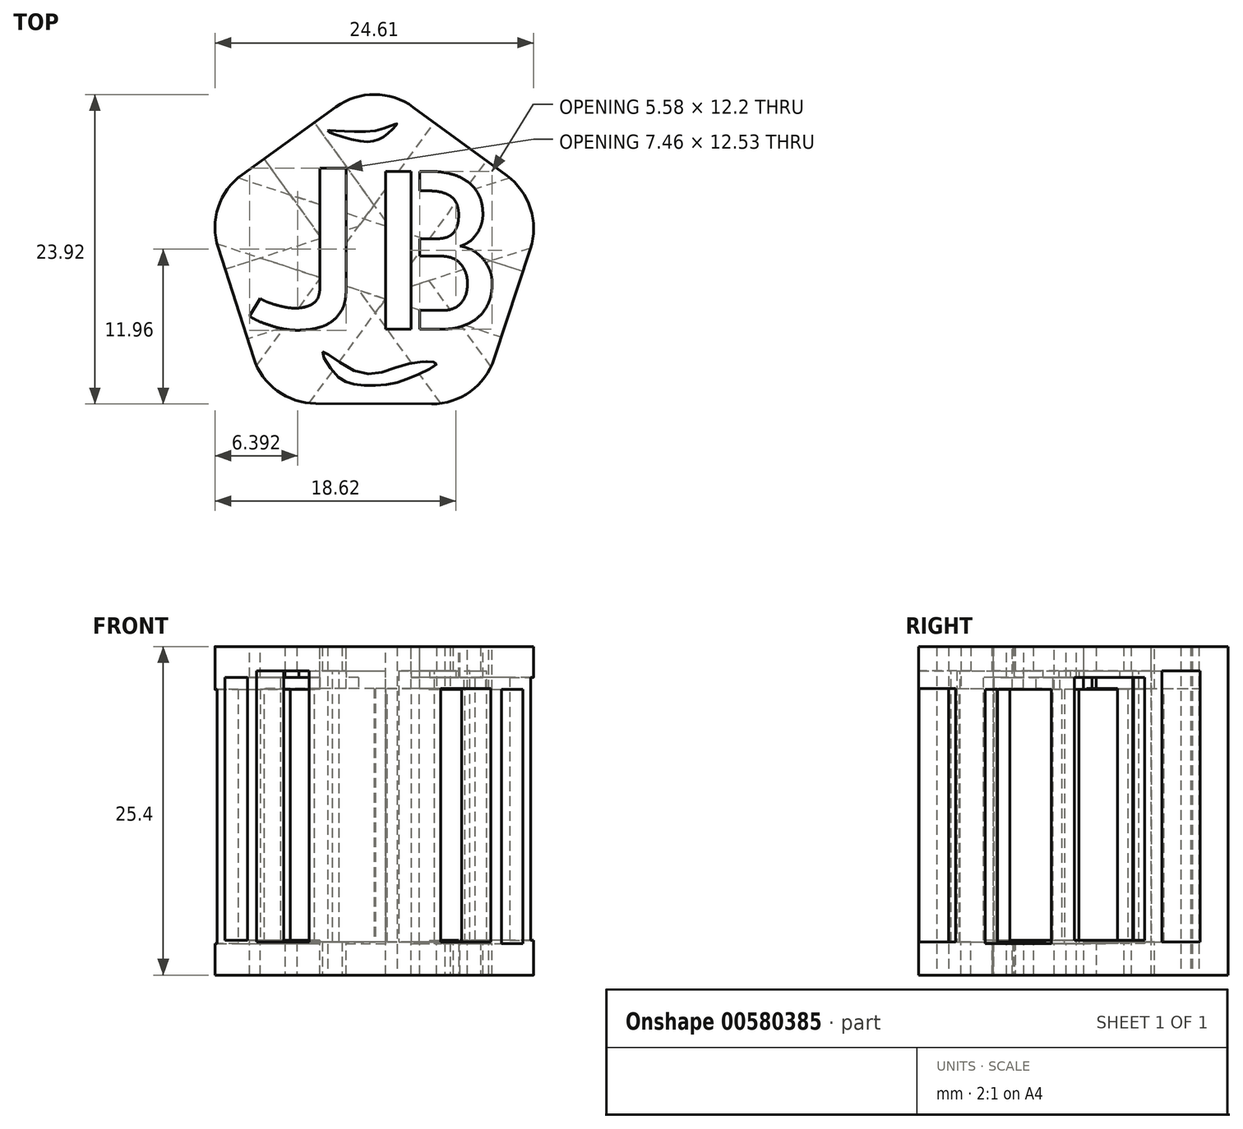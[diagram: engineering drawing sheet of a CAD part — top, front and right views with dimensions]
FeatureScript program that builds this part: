
annotation { "Feature Type Name" : "Feature", "Feature Type Description" : "" }
export const myFeature = defineFeature(function(context is Context, id is Id, definition is map)
    precondition{}
    {
        {
            var Q0;
            Q0=qCreatedBy(makeId("Top.planeOp"),FACE);
            var sketch = newSketch(context, id + "F0", { "sketchPlane" : qUnion([Q0])});
            skLineSegment(sketch, "E0.bottom", {"start": v(-11.35, 8.5) * mm, "end": v(14.05, 8.5) * mm});
            skLineSegment(sketch, "E0.top", {"start": v(-11.35, -16.9) * mm, "end": v(14.05, -16.9) * mm});
            skLineSegment(sketch, "E0.left", {"start": v(-11.35, 8.5) * mm, "end": v(-11.35, -16.9) * mm});
            skLineSegment(sketch, "E0.right", {"start": v(14.05, 8.5) * mm, "end": v(14.05, -16.9) * mm});
            skSolve(sketch);
        }
        {
            var Q0;
            Q0=makeQuery(id+"F0.imprint","IMPRINT",FACE,{"disambiguationData":[TD([[makeQuery(id+"F0.imprint","IMPRINT",EDGE,{"derivedFrom":sQuery(id+"F0.wireOp",EDGE,"E0.bottom")}),-1.0]])]});
            var sketch = newSketch(context, id + "F1", { "sketchPlane" : qUnion([Q0])});
            skCircle(sketch, "E1.cCircle", {"center": v(0, -4.14) * mm, "radius": 11.23 * mm, "construction": true});
            skLineSegment(sketch, "E1.0", {"start": v(0.05, 9.74) * mm, "end": v(13.21, 0.1) * mm});
            skLineSegment(sketch, "E1.1", {"start": v(13.21, 0.1) * mm, "end": v(8.12, -15.4) * mm});
            skLineSegment(sketch, "E1.2", {"start": v(8.12, -15.4) * mm, "end": v(-8.2, -15.34) * mm});
            skLineSegment(sketch, "E1.3", {"start": v(-8.2, -15.34) * mm, "end": v(-13.18, 0.2) * mm});
            skLineSegment(sketch, "E1.4", {"start": v(-13.18, 0.2) * mm, "end": v(0.05, 9.74) * mm});
            skPoint(sketch, "E1.0.midPoint", {"position": v(6.63, 4.92) * mm});
            skSolve(sketch);
        }
        {
            var Q0;
            Q0 = qSketchRegion(id + "F1", true);
            extrude(context, id + "F2", {"entities" : qUnion([Q0]), "depth" : 25.4 * mm, "offsetDistance" : 25.4 * mm});
        }
        {
            var Q0;
            Q0=makeQuery(id+"F2.opExtrude","CAP_FACE",FACE,{"disambiguationData":[OSD([sQuery(id+"F1.wireOp",EDGE,"E1.0"),sQuery(id+"F1.wireOp",EDGE,"E1.1"),sQuery(id+"F1.wireOp",EDGE,"E1.2"),sQuery(id+"F1.wireOp",EDGE,"E1.3"),sQuery(id+"F1.wireOp",EDGE,"E1.4")])],"isStart":false});
            var sketch = newSketch(context, id + "F3", { "sketchPlane" : qUnion([Q0])});
            skText(sketch, "E2", { "text": "JB", "fontName": "AllertaStencil-Regular.ttf"});
            const initialGuessF3  = {"E2": [-0.01007, -0.0096, 1, 0, 0.0122]};
            skSetInitialGuess(sketch, initialGuessF3);
            skSolve(sketch);
        }
        {
            var Q0;
            Q0 = qSketchRegion(id + "F3", true);
            extrude(context, id + "F4", {"entities" : qUnion([Q0]), "operationType" : NewBodyOperationType.REMOVE, "oppositeDirection" : true, "depth" : 25.4 * mm, "offsetDistance" : 25.4 * mm});
        }
        {
            var Q0;
            Q0=makeQuery(id+"F2.opExtrude","CAP_FACE",FACE,{"disambiguationData":[OSD([sQuery(id+"F1.wireOp",EDGE,"E1.0"),sQuery(id+"F1.wireOp",EDGE,"E1.1"),sQuery(id+"F1.wireOp",EDGE,"E1.2"),sQuery(id+"F1.wireOp",EDGE,"E1.3"),sQuery(id+"F1.wireOp",EDGE,"E1.4")])],"isStart":false});
            var sketch = newSketch(context, id + "F5", { "sketchPlane" : qUnion([Q0])});
            skFitSpline(sketch, "E3", {"points": [v(-3.6, 5.74) * mm, v(-1.01, 4.93) * mm, v(0.87, 5.38) * mm, v(1.76, 6.27) * mm, v(0, 5.74) * mm, v(-3.6, 5.74) * mm]});
            skSolve(sketch);
        }
        {
            var Q0;
            Q0 = qSketchRegion(id + "F5", true);
            extrude(context, id + "F6", {"entities" : qUnion([Q0]), "operationType" : NewBodyOperationType.REMOVE, "endBound" : BoundingType.THROUGH_ALL, "oppositeDirection" : true, "depth" : 25.4 * mm, "offsetDistance" : 25.4 * mm});
        }
        {
            var Q0;
            Q0=makeQuery(id+"F2.opExtrude","CAP_FACE",FACE,{"disambiguationData":[OSD([sQuery(id+"F1.wireOp",EDGE,"E1.0"),sQuery(id+"F1.wireOp",EDGE,"E1.1"),sQuery(id+"F1.wireOp",EDGE,"E1.2"),sQuery(id+"F1.wireOp",EDGE,"E1.3"),sQuery(id+"F1.wireOp",EDGE,"E1.4")])],"isStart":false});
            var sketch = newSketch(context, id + "F7", { "sketchPlane" : qUnion([Q0])});
            skFitSpline(sketch, "E4", {"points": [v(-3.99, -11.35) * mm, v(-3, -13.08) * mm, v(-1.58, -13.84) * mm, v(0.83, -13.91) * mm, v(3.23, -13.16) * mm, v(4.81, -12.26) * mm, v(2.7, -12.26) * mm, v(-1.2, -12.93) * mm, v(-3.99, -11.35) * mm]});
            skSolve(sketch);
        }
        {
            var Q0;
            Q0 = qSketchRegion(id + "F7", true);
            extrude(context, id + "F8", {"entities" : qUnion([Q0]), "operationType" : NewBodyOperationType.REMOVE, "endBound" : BoundingType.THROUGH_ALL, "oppositeDirection" : true, "depth" : 25.4 * mm, "offsetDistance" : 25.4 * mm});
        }
        {
            var Q0;
            Q0=makeQuery(id+"F2.opExtrude","SWEPT_EDGE",EDGE,{"disambiguationData":[OSD([sQuery(id+"F1.wireOp",EDGE,"E1.3"),sQuery(id+"F1.wireOp",EDGE,"E1.4")])]});
            var Q1;
            Q1=makeQuery(id+"F2.opExtrude","SWEPT_EDGE",EDGE,{"disambiguationData":[OSD([sQuery(id+"F1.wireOp",EDGE,"E1.2"),sQuery(id+"F1.wireOp",EDGE,"E1.3")])]});
            var Q2;
            Q2=makeQuery(id+"F2.opExtrude","SWEPT_EDGE",EDGE,{"disambiguationData":[OSD([sQuery(id+"F1.wireOp",EDGE,"E1.1"),sQuery(id+"F1.wireOp",EDGE,"E1.2")])]});
            var Q3;
            Q3=makeQuery(id+"F2.opExtrude","SWEPT_EDGE",EDGE,{"disambiguationData":[OSD([sQuery(id+"F1.wireOp",EDGE,"E1.0"),sQuery(id+"F1.wireOp",EDGE,"E1.1")])]});
            var Q4;
            Q4=makeQuery(id+"F2.opExtrude","SWEPT_EDGE",EDGE,{"disambiguationData":[OSD([sQuery(id+"F1.wireOp",EDGE,"E1.0"),sQuery(id+"F1.wireOp",EDGE,"E1.4")])]});
            fillet(context, id + "F9", {"entities" : qUnion([Q0, Q1, Q2, Q3, Q4]), "radius" : 5.08 * mm, "tangentPropagation" : true, "allowEdgeOverflow" : false});
        }
        {
            var Q0;
            Q0=makeQuery(id+"F2.opExtrude","SWEPT_FACE",FACE,{"disambiguationData":[OSD([sQuery(id+"F1.wireOp",EDGE,"E1.3")])]});
            var sketch = newSketch(context, id + "F10", { "sketchPlane" : qUnion([Q0])});
            skLineSegment(sketch, "E5.bottom", {"start": v(1.21, 2.68) * mm, "end": v(6.87, 2.68) * mm});
            skLineSegment(sketch, "E5.top", {"start": v(1.21, 23.02) * mm, "end": v(6.87, 23.02) * mm});
            skLineSegment(sketch, "E5.left", {"start": v(1.21, 2.68) * mm, "end": v(1.21, 23.02) * mm});
            skLineSegment(sketch, "E5.right", {"start": v(6.87, 2.68) * mm, "end": v(6.87, 23.02) * mm});
            skSolve(sketch);
        }
        {
            var Q0;
            Q0 = qSketchRegion(id + "F10", true);
            extrude(context, id + "F11", {"entities" : qUnion([Q0]), "operationType" : NewBodyOperationType.REMOVE, "endBound" : BoundingType.THROUGH_ALL, "oppositeDirection" : true, "depth" : 25.4 * mm, "offsetDistance" : 25.4 * mm});
        }
        {
            var Q0;
            Q0=makeQuery(id+"F2.opExtrude","SWEPT_FACE",FACE,{"disambiguationData":[OSD([sQuery(id+"F1.wireOp",EDGE,"E1.1")])]});
            var sketch = newSketch(context, id + "F12", { "sketchPlane" : qUnion([Q0])});
            skLineSegment(sketch, "E6.bottom", {"start": v(-1.28, 22.08) * mm, "end": v(-6.63, 22.08) * mm});
            skLineSegment(sketch, "E6.top", {"start": v(-1.28, 2.43) * mm, "end": v(-6.63, 2.43) * mm});
            skLineSegment(sketch, "E6.left", {"start": v(-1.28, 22.08) * mm, "end": v(-1.28, 2.43) * mm});
            skLineSegment(sketch, "E6.right", {"start": v(-6.63, 22.08) * mm, "end": v(-6.63, 2.43) * mm});
            skSolve(sketch);
        }
        {
            var Q0;
            Q0 = qSketchRegion(id + "F12", true);
            extrude(context, id + "F13", {"entities" : qUnion([Q0]), "operationType" : NewBodyOperationType.REMOVE, "endBound" : BoundingType.THROUGH_ALL, "oppositeDirection" : true, "depth" : 25.4 * mm, "offsetDistance" : 25.4 * mm});
        }
        {
            var Q0;
            Q0=makeQuery(id+"F2.opExtrude","SWEPT_FACE",FACE,{"disambiguationData":[OSD([sQuery(id+"F1.wireOp",EDGE,"E1.4")])]});
            var sketch = newSketch(context, id + "F14", { "sketchPlane" : qUnion([Q0])});
            skLineSegment(sketch, "E7.bottom", {"start": v(4.8, 2.55) * mm, "end": v(0, 2.55) * mm});
            skLineSegment(sketch, "E7.top", {"start": v(4.8, 22.13) * mm, "end": v(0, 22.13) * mm});
            skLineSegment(sketch, "E7.left", {"start": v(4.8, 2.55) * mm, "end": v(4.8, 22.13) * mm});
            skLineSegment(sketch, "E7.right", {"start": v(0, 2.55) * mm, "end": v(0, 22.13) * mm});
            skSolve(sketch);
        }
        {
            var Q0;
            Q0 = qSketchRegion(id + "F14", true);
            extrude(context, id + "F15", {"entities" : qUnion([Q0]), "operationType" : NewBodyOperationType.REMOVE, "endBound" : BoundingType.THROUGH_ALL, "oppositeDirection" : true, "depth" : 25.4 * mm, "offsetDistance" : 25.4 * mm});
        }
        {
            var Q0;
            Q0=makeQuery(id+"F2.opExtrude","SWEPT_FACE",FACE,{"disambiguationData":[OSD([sQuery(id+"F1.wireOp",EDGE,"E1.0")])]});
            var sketch = newSketch(context, id + "F16", { "sketchPlane" : qUnion([Q0])});
            skLineSegment(sketch, "E8.bottom", {"start": v(0, 2.57) * mm, "end": v(-5, 2.57) * mm});
            skLineSegment(sketch, "E8.top", {"start": v(0, 23.51) * mm, "end": v(-5, 23.51) * mm});
            skLineSegment(sketch, "E8.left", {"start": v(0, 2.57) * mm, "end": v(0, 23.51) * mm});
            skLineSegment(sketch, "E8.right", {"start": v(-5, 2.57) * mm, "end": v(-5, 23.51) * mm});
            skSolve(sketch);
        }
        {
            var Q0;
            Q0 = qSketchRegion(id + "F16", true);
            extrude(context, id + "F17", {"entities" : qUnion([Q0]), "operationType" : NewBodyOperationType.REMOVE, "endBound" : BoundingType.THROUGH_ALL, "oppositeDirection" : true, "depth" : 25.4 * mm, "offsetDistance" : 25.4 * mm});
        }
    });
